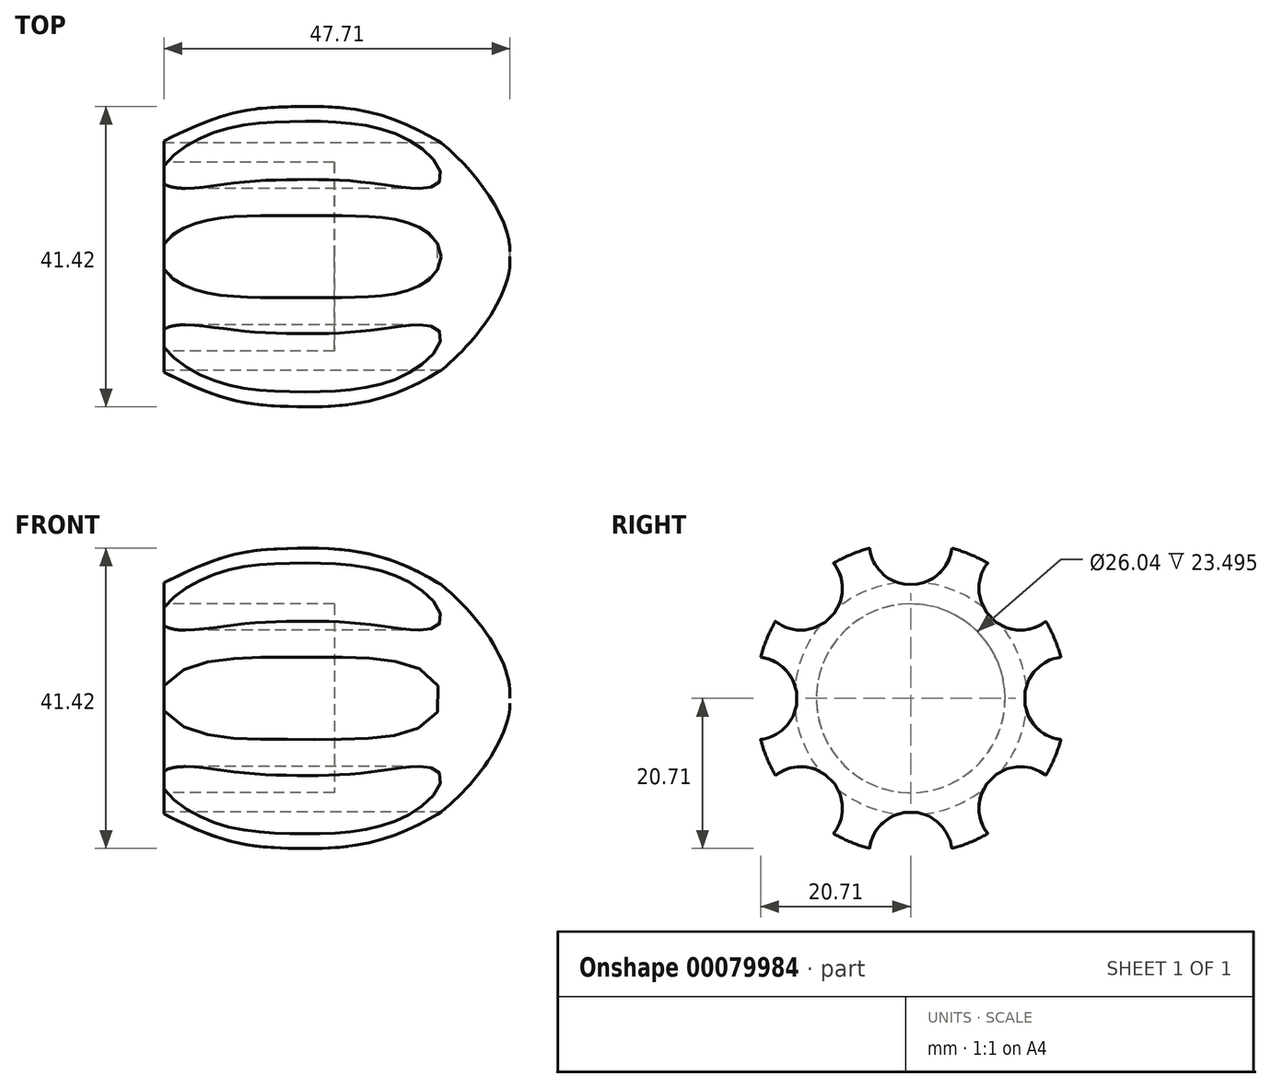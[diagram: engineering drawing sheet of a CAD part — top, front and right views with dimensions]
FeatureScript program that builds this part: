
annotation { "Feature Type Name" : "Feature", "Feature Type Description" : "" }
export const myFeature = defineFeature(function(context is Context, id is Id, definition is map)
    precondition{}
    {
        {
            var Q0;
            Q0=qCreatedBy(makeId("Front.planeOp"),FACE);
            var sketch = newSketch(context, id + "F0", { "sketchPlane" : qUnion([Q0])});
            skLineSegment(sketch, "E0.right", {"start": v(-22.72, 16.04) * mm, "end": v(-22.73, 13.02) * mm});
            skPoint(sketch, "E0.middle", {"position": v(0, 0) * mm});
            skLineSegment(sketch, "E1.top", {"start": v(0.76, 13.02) * mm, "end": v(-22.73, 13.02) * mm});
            skLineSegment(sketch, "E1.left", {"start": v(0.76, 0) * mm, "end": v(0.76, 13.02) * mm});
            skLineSegment(sketch, "E2.left", {"start": v(-22.73, 13.02) * mm, "end": v(-22.72, 16.04) * mm});
            skLineSegment(sketch, "E3", {"start": v(0, 0) * mm, "end": v(0.76, 0) * mm});
            skFitSpline(sketch, "E4", {"points": [v(-22.72, 16.04) * mm, v(-5.07, 21.44) * mm, v(12.42, 17.87) * mm, v(24.95, 0) * mm, v(-22.72, -16.04) * mm], "startDerivative": vector(105.94, 70.15) * mm, "endDerivative": vector(-254.66, -58.47) * mm});
            skLineSegment(sketch, "E5", {"start": v(0.76, 0) * mm, "end": v(24.95, 0) * mm});
            skSolve(sketch);
        }
        {
            var Q0;
            Q0=makeQuery(id+"F0.imprint","IMPRINT",FACE,{"disambiguationData":[TD([[makeQuery(id+"F0.imprint","IMPRINT",EDGE,{"derivedFrom":sQuery(id+"F0.wireOp",EDGE,"E1.top")}),-1.0]])]});
            var Q1;
            Q1=sQuery(id+"F0.wireOp",EDGE,"E5");
            revolve(context, id + "F1", {"entities" : qUnion([Q0]), "axis" : qUnion([Q1]), "revolveType" : RevolveType.FULL});
        }
        {
            var Q0;
            Q0=qCreatedBy(makeId("Right.planeOp"),FACE);
            var sketch = newSketch(context, id + "F2", { "sketchPlane" : qUnion([Q0])});
            skCircle(sketch, "E6", {"center": v(0, 21.4) * mm, "radius": 5.72 * mm});
            skCircle(sketch, "E7.1.0", {"center": v(-15.13, 15.13) * mm, "radius": 5.71 * mm});
            skPoint(sketch, "E7.center", {"position": v(0, 0) * mm});
            skCircle(sketch, "E8.1.2.0", {"center": v(-21.4, 0) * mm, "radius": 5.72 * mm});
            skCircle(sketch, "E8.1.3.0", {"center": v(-15.13, -15.13) * mm, "radius": 5.72 * mm});
            skCircle(sketch, "E8.1.4.0", {"center": v(0, -21.4) * mm, "radius": 5.72 * mm});
            skCircle(sketch, "E8.1.5.0", {"center": v(15.13, -15.13) * mm, "radius": 5.72 * mm});
            skCircle(sketch, "E8.1.6.0", {"center": v(21.4, 0) * mm, "radius": 5.72 * mm});
            skCircle(sketch, "E8.1.7.0", {"center": v(15.13, 15.13) * mm, "radius": 5.72 * mm});
            skSolve(sketch);
        }
        {
            var Q0;
            Q0=makeQuery(id+"F2.imprint","IMPRINT",FACE,{"disambiguationData":[TD([[makeQuery(id+"F2.imprint","IMPRINT",EDGE,{"derivedFrom":sQuery(id+"F2.wireOp",EDGE,"E7.1.0")}),1.0]])]});
            var Q1;
            Q1=makeQuery(id+"F2.imprint","IMPRINT",FACE,{"disambiguationData":[TD([[makeQuery(id+"F2.imprint","IMPRINT",EDGE,{"derivedFrom":sQuery(id+"F2.wireOp",EDGE,"E8.1.2.0")}),1.0]])]});
            var Q2;
            Q2=makeQuery(id+"F2.imprint","IMPRINT",FACE,{"disambiguationData":[TD([[makeQuery(id+"F2.imprint","IMPRINT",EDGE,{"derivedFrom":sQuery(id+"F2.wireOp",EDGE,"E8.1.3.0")}),1.0]])]});
            var Q3;
            Q3=makeQuery(id+"F2.imprint","IMPRINT",FACE,{"disambiguationData":[TD([[makeQuery(id+"F2.imprint","IMPRINT",EDGE,{"derivedFrom":sQuery(id+"F2.wireOp",EDGE,"E8.1.4.0")}),1.0]])]});
            var Q4;
            Q4=makeQuery(id+"F2.imprint","IMPRINT",FACE,{"disambiguationData":[TD([[makeQuery(id+"F2.imprint","IMPRINT",EDGE,{"derivedFrom":sQuery(id+"F2.wireOp",EDGE,"E8.1.5.0")}),1.0]])]});
            var Q5;
            Q5=makeQuery(id+"F2.imprint","IMPRINT",FACE,{"disambiguationData":[TD([[makeQuery(id+"F2.imprint","IMPRINT",EDGE,{"derivedFrom":sQuery(id+"F2.wireOp",EDGE,"E8.1.6.0")}),1.0]])]});
            var Q6;
            Q6=makeQuery(id+"F2.imprint","IMPRINT",FACE,{"disambiguationData":[TD([[makeQuery(id+"F2.imprint","IMPRINT",EDGE,{"derivedFrom":sQuery(id+"F2.wireOp",EDGE,"E6")}),1.0]])]});
            var Q7;
            Q7=makeQuery(id+"F2.imprint","IMPRINT",FACE,{"disambiguationData":[TD([[makeQuery(id+"F2.imprint","IMPRINT",EDGE,{"derivedFrom":sQuery(id+"F2.wireOp",EDGE,"E8.1.7.0")}),1.0]])]});
            extrude(context, id + "F3", {"entities" : qUnion([Q0, Q1, Q2, Q3, Q4, Q5, Q6, Q7]), "operationType" : NewBodyOperationType.REMOVE, "endBound" : BoundingType.THROUGH_ALL, "depth" : 25.4 * mm, "hasSecondDirection" : true, "secondDirectionOppositeDirection" : true, "secondDirectionDepth" : 25.4 * mm});
        }
    });
